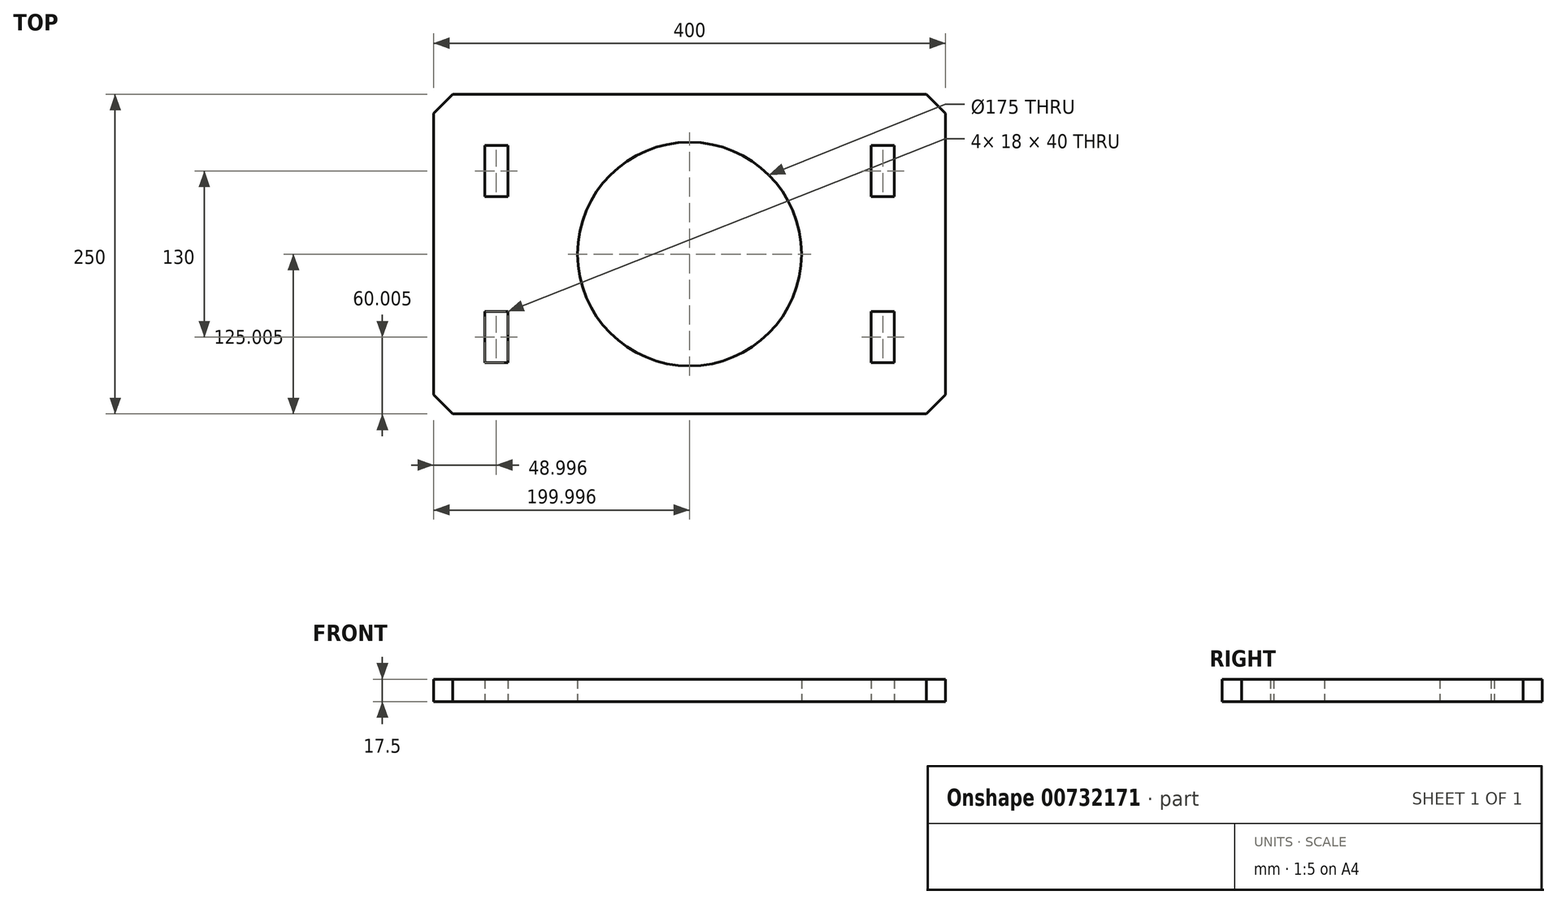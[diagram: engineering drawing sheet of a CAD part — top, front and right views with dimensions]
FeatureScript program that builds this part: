
annotation { "Feature Type Name" : "Feature", "Feature Type Description" : "" }
export const myFeature = defineFeature(function(context is Context, id is Id, definition is map)
    precondition{}
    {
        {
            var Q0;
            Q0=qCreatedBy(makeId("Top.planeOp"),FACE);
            var sketch = newSketch(context, id + "F0", { "sketchPlane" : qUnion([Q0])});
            skLineSegment(sketch, "E0.bottom", {"start": v(-307.21, 167.97) * mm, "end": v(92.79, 167.97) * mm});
            skLineSegment(sketch, "E0.top", {"start": v(-307.21, -82.03) * mm, "end": v(92.79, -82.03) * mm});
            skLineSegment(sketch, "E0.left", {"start": v(-307.21, 167.97) * mm, "end": v(-307.21, -82.03) * mm});
            skLineSegment(sketch, "E0.right", {"start": v(92.79, 167.97) * mm, "end": v(92.79, -82.03) * mm});
            skCircle(sketch, "E1", {"center": v(-107.21, 42.97) * mm, "radius": 87.5 * mm});
            skLineSegment(sketch, "E2.bottom", {"start": v(-267.21, 127.97) * mm, "end": v(-249.21, 127.97) * mm});
            skLineSegment(sketch, "E2.top", {"start": v(-267.21, 87.97) * mm, "end": v(-249.21, 87.97) * mm});
            skLineSegment(sketch, "E2.left", {"start": v(-267.21, 127.97) * mm, "end": v(-267.21, 87.97) * mm});
            skLineSegment(sketch, "E2.right", {"start": v(-249.21, 127.97) * mm, "end": v(-249.21, 87.97) * mm});
            skLineSegment(sketch, "E3.bottom", {"start": v(-267.21, -2.03) * mm, "end": v(-249.21, -2.03) * mm});
            skLineSegment(sketch, "E3.top", {"start": v(-267.21, -42.03) * mm, "end": v(-249.21, -42.03) * mm});
            skLineSegment(sketch, "E3.left", {"start": v(-267.21, -2.03) * mm, "end": v(-267.21, -42.03) * mm});
            skLineSegment(sketch, "E3.right", {"start": v(-249.21, -2.03) * mm, "end": v(-249.21, -42.03) * mm});
            skLineSegment(sketch, "E4.bottom", {"start": v(34.79, 127.97) * mm, "end": v(52.79, 127.97) * mm});
            skLineSegment(sketch, "E4.top", {"start": v(34.79, 87.97) * mm, "end": v(52.79, 87.97) * mm});
            skLineSegment(sketch, "E4.left", {"start": v(34.79, 127.97) * mm, "end": v(34.79, 87.97) * mm});
            skLineSegment(sketch, "E4.right", {"start": v(52.79, 127.97) * mm, "end": v(52.79, 87.97) * mm});
            skLineSegment(sketch, "E5.bottom", {"start": v(34.79, -2.03) * mm, "end": v(52.79, -2.03) * mm});
            skLineSegment(sketch, "E5.top", {"start": v(34.79, -42.03) * mm, "end": v(52.79, -42.03) * mm});
            skLineSegment(sketch, "E5.left", {"start": v(34.79, -2.03) * mm, "end": v(34.79, -42.03) * mm});
            skLineSegment(sketch, "E5.right", {"start": v(52.79, -2.03) * mm, "end": v(52.79, -42.03) * mm});
            skLineSegment(sketch, "E6", {"start": v(-307.21, 167.97) * mm, "end": v(92.79, -82.03) * mm, "construction": true});
            skLineSegment(sketch, "E7", {"start": v(92.79, 167.97) * mm, "end": v(-307.21, -82.03) * mm, "construction": true});
            skSolve(sketch);
        }
        {
            var Q0;
            Q0 = qSketchRegion(id + "F0", true);
            extrude(context, id + "F1", {"entities" : qUnion([Q0]), "depth" : 17.5 * mm, "offsetDistance" : 25 * mm});
        }
        {
            var Q0;
            Q0=makeQuery(id+"F1.opExtrude","SWEPT_EDGE",EDGE,{"disambiguationData":[OSD([sQuery(id+"F0.wireOp",EDGE,"E0.bottom"),sQuery(id+"F0.wireOp",EDGE,"E0.left")])]});
            var Q1;
            Q1=makeQuery(id+"F1.opExtrude","SWEPT_EDGE",EDGE,{"disambiguationData":[OSD([sQuery(id+"F0.wireOp",EDGE,"E0.bottom"),sQuery(id+"F0.wireOp",EDGE,"E0.right")])]});
            var Q2;
            Q2=makeQuery(id+"F1.opExtrude","SWEPT_EDGE",EDGE,{"disambiguationData":[OSD([sQuery(id+"F0.wireOp",EDGE,"E0.top"),sQuery(id+"F0.wireOp",EDGE,"E0.right")])]});
            var Q3;
            Q3=makeQuery(id+"F1.opExtrude","SWEPT_EDGE",EDGE,{"disambiguationData":[OSD([sQuery(id+"F0.wireOp",EDGE,"E0.top"),sQuery(id+"F0.wireOp",EDGE,"E0.left")])]});
            chamfer(context, id + "F2", {"entities" : qUnion([Q0, Q1, Q2, Q3]), "width" : 15 * mm, "tangentPropagation" : true});
        }
    });
